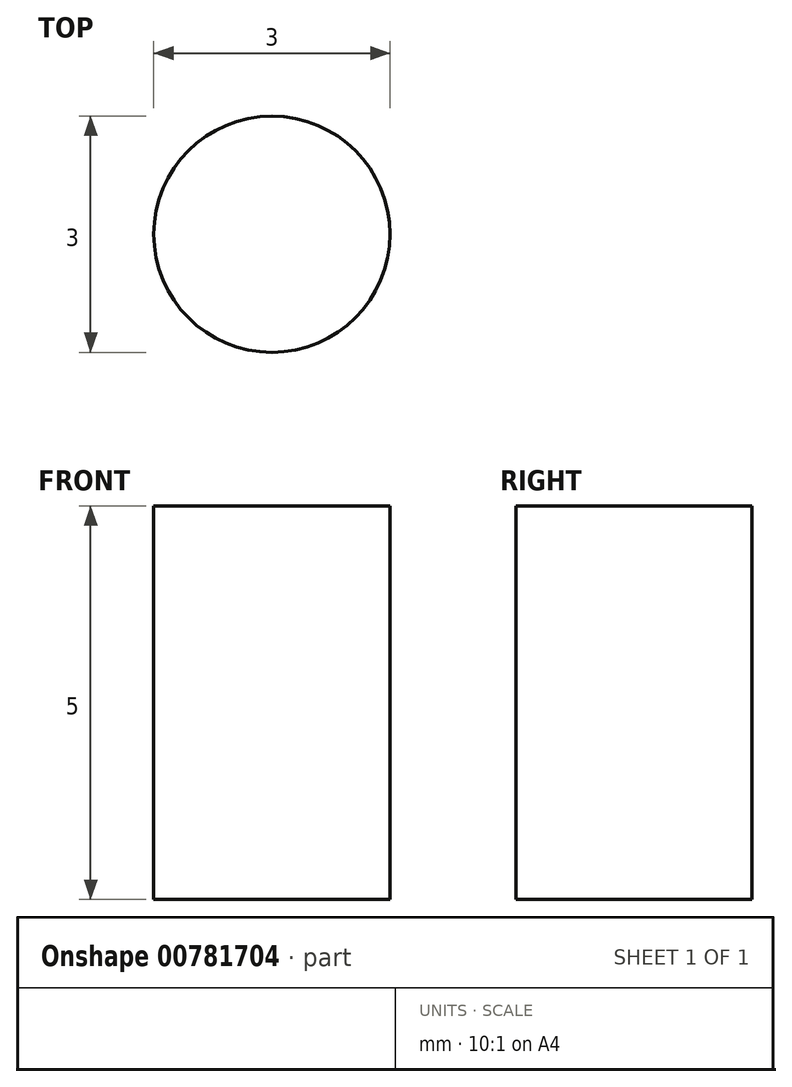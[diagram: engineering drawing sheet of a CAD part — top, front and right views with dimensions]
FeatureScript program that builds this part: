
annotation { "Feature Type Name" : "Feature", "Feature Type Description" : "" }
export const myFeature = defineFeature(function(context is Context, id is Id, definition is map)
    precondition{}
    {
        {
            var Q0;
            Q0=qCreatedBy(makeId("Top.planeOp"),FACE);
            var sketch = newSketch(context, id + "F0", { "sketchPlane" : qUnion([Q0])});
            skCircle(sketch, "E0", {"center": v(0, 0) * mm, "radius": 1.5 * mm});
            skSolve(sketch);
        }
        {
            var Q0;
            Q0=makeQuery(id+"F0.imprint","IMPRINT",FACE,{"disambiguationData":[TD([[makeQuery(id+"F0.imprint","IMPRINT",EDGE,{"derivedFrom":sQuery(id+"F0.wireOp",EDGE,"E0")}),1.0]])]});
            extrude(context, id + "F1", {"entities" : qUnion([Q0]), "depth" : 5 * mm, "offsetDistance" : 25 * mm});
        }
    });
